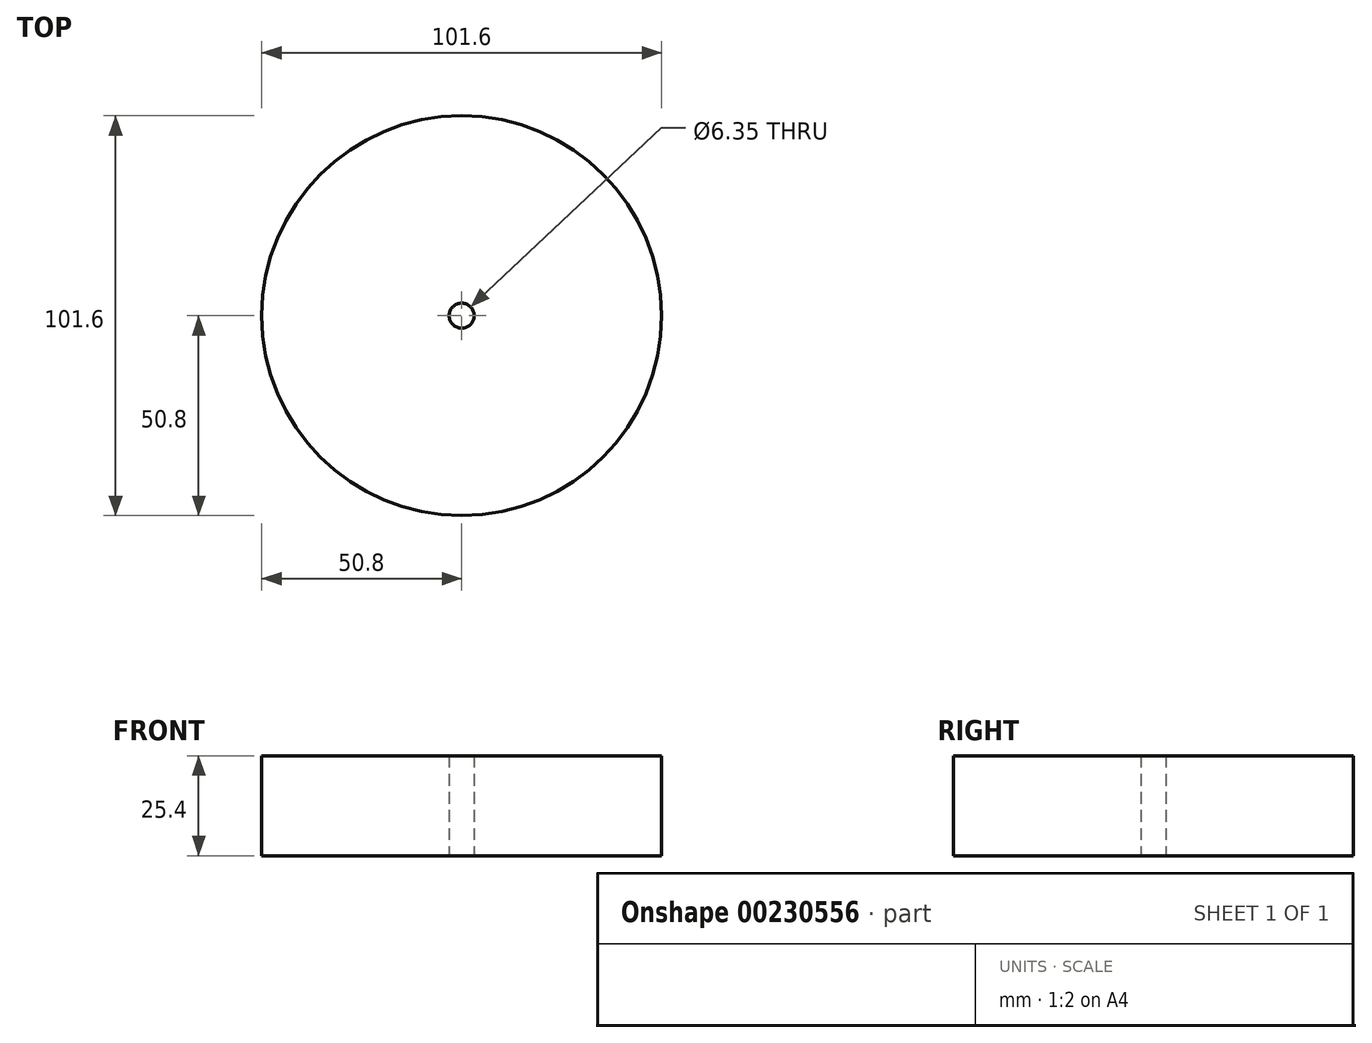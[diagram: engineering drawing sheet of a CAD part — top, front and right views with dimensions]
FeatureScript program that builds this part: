
annotation { "Feature Type Name" : "Feature", "Feature Type Description" : "" }
export const myFeature = defineFeature(function(context is Context, id is Id, definition is map)
    precondition{}
    {
        {
            var Q0;
            Q0=qCreatedBy(makeId("Top.planeOp"),FACE);
            var sketch = newSketch(context, id + "F0", { "sketchPlane" : qUnion([Q0])});
            skCircle(sketch, "E0", {"center": v(0, 0) * mm, "radius": 50.8 * mm});
            skCircle(sketch, "E1", {"center": v(0, 0) * mm, "radius": 3.18 * mm});
            skSolve(sketch);
        }
        {
            var Q0;
            Q0 = qSketchRegion(id + "F0", true);
            extrude(context, id + "F1", {"entities" : qUnion([Q0]), "depth" : 25.4 * mm});
        }
    });
